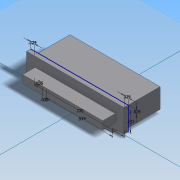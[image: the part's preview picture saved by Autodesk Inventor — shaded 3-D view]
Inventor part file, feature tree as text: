
AUTODESK INVENTOR PART (.ipt)
format: ipt  version: 2014 SP2 (Build 180246200, 246)  size: 113,664 bytes
history: native  units: in
note: dims shown in document units (in); Inventor stores cm internally (conversion verified against a paired STEP export)
features: extrude x4, sketch x2
ambient origin geometry x8: Origin, YZ Plane, XZ Plane, XY Plane, X Axis, Y Axis, Z Axis, Center Point
bodies: Solid1 (feature_tree)
feature tree (6):
  sketch  "Sketch1"  dims[d0=0.72in d1=0.157in]
  extrude  "Extrusion1"  Depth=0.157in
  extrude  "Extrusion2"  Depth=0.029in
  extrude  "Extrusion3"  Depth=0.029in
  extrude  "Extrusion4"  Depth=0.029in
  sketch  "Sketch2"  dims[d2=0.284in d3=0.0in d4=0.029in d6=0.029in d7=0.029in d8=0.034in d9=0.0in d10=0.64in d11=0.063in d12=0.1in d13=0.0in d14=0.03in d16=0.035in d17=0.534in d18=0.218in d19=0.0in]
